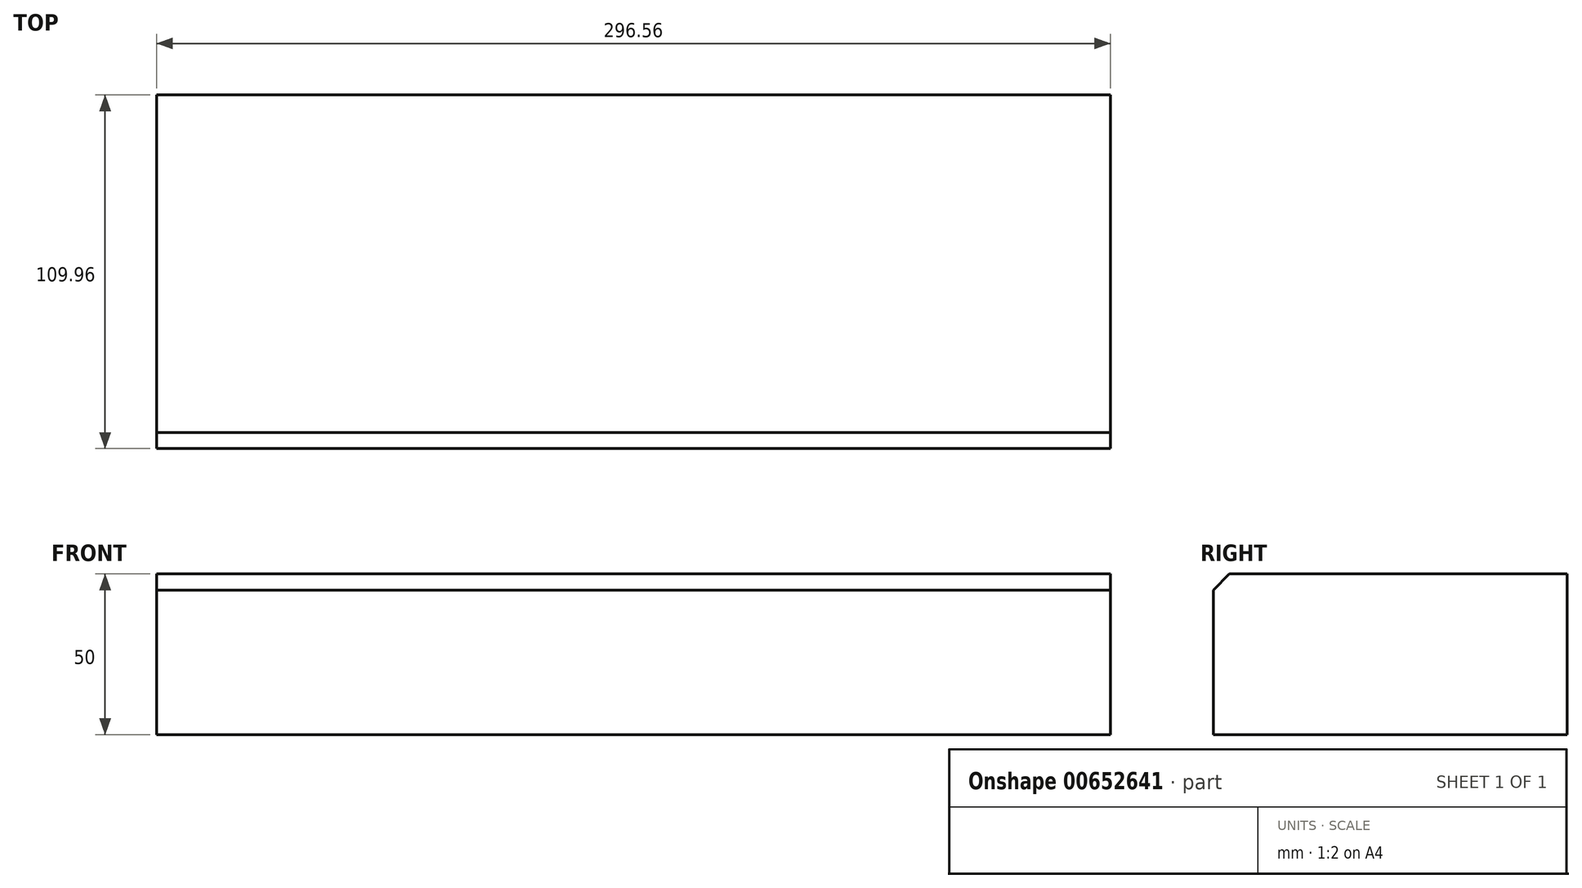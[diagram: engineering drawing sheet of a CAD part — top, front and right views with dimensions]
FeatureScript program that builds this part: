
annotation { "Feature Type Name" : "Feature", "Feature Type Description" : "" }
export const myFeature = defineFeature(function(context is Context, id is Id, definition is map)
    precondition{}
    {
        {
            var Q0;
            Q0=qCreatedBy(makeId("Top.planeOp"),FACE);
            var sketch = newSketch(context, id + "F0", { "sketchPlane" : qUnion([Q0])});
            skLineSegment(sketch, "E0.bottom", {"start": v(-148.28, 54.98) * mm, "end": v(148.28, 54.98) * mm});
            skLineSegment(sketch, "E0.top", {"start": v(-148.28, -54.98) * mm, "end": v(148.28, -54.98) * mm});
            skLineSegment(sketch, "E0.left", {"start": v(-148.28, 54.98) * mm, "end": v(-148.28, -54.98) * mm});
            skLineSegment(sketch, "E0.right", {"start": v(148.28, 54.98) * mm, "end": v(148.28, -54.98) * mm});
            skPoint(sketch, "E0.middle", {"position": v(0, 0) * mm});
            skSolve(sketch);
        }
        {
            var Q0;
            Q0 = qSketchRegion(id + "F0", true);
            extrude(context, id + "F1", {"entities" : qUnion([Q0]), "depth" : 25 * mm, "offsetDistance" : 25 * mm, "hasDraft" : true, "draftAngle" : 0 * degree, "hasSecondDirection" : true, "secondDirectionOppositeDirection" : true, "secondDirectionDepth" : 25 * mm, "hasSecondDirectionDraft" : true, "secondDirectionDraftAngle" : 0 * degree});
        }
        {
            var Q0;
            Q0=makeQuery(id+"F1.opExtrude","CAP_EDGE",EDGE,{"disambiguationData":[OSD([sQuery(id+"F0.wireOp",EDGE,"E0.top")])],"isStart":false});
            chamfer(context, id + "F2", {"entities" : qUnion([Q0]), "chamferType" : ChamferType.OFFSET_ANGLE, "width" : 5 * mm, "oppositeDirection" : false, "angle" : 45 * degree, "tangentPropagation" : true});
        }
    });
